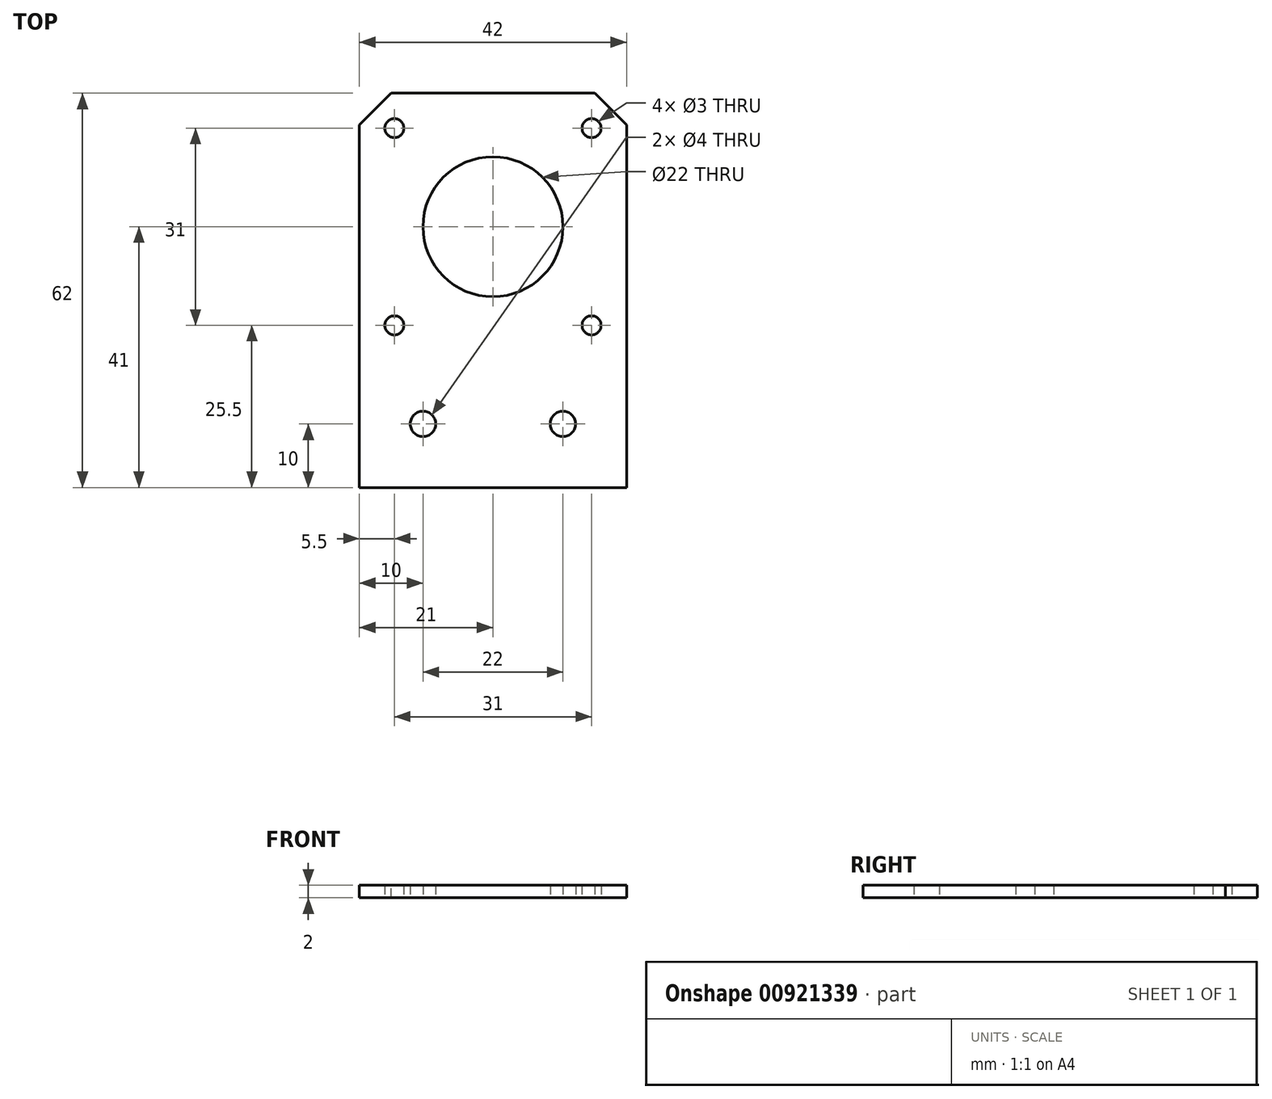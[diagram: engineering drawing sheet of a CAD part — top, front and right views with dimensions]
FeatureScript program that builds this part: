
annotation { "Feature Type Name" : "Feature", "Feature Type Description" : "" }
export const myFeature = defineFeature(function(context is Context, id is Id, definition is map)
    precondition{}
    {
        {
            var Q0;
            Q0=qCreatedBy(makeId("Top.planeOp"),FACE);
            var sketch = newSketch(context, id + "F0", { "sketchPlane" : qUnion([Q0])});
            skLineSegment(sketch, "E0.bottom", {"start": v(21, -31) * mm, "end": v(-21, -31) * mm});
            skLineSegment(sketch, "E0.top", {"start": v(21, 31) * mm, "end": v(-21, 31) * mm});
            skLineSegment(sketch, "E0.left", {"start": v(21, -31) * mm, "end": v(21, 31) * mm});
            skLineSegment(sketch, "E0.right", {"start": v(-21, -31) * mm, "end": v(-21, 31) * mm});
            skPoint(sketch, "E0.middle", {"position": v(0, 0) * mm});
            skCircle(sketch, "E1", {"center": v(-11, -21) * mm, "radius": 2 * mm});
            skCircle(sketch, "E2", {"center": v(11, -21) * mm, "radius": 2 * mm});
            skCircle(sketch, "E3", {"center": v(0, 10) * mm, "radius": 11 * mm});
            skCircle(sketch, "E4", {"center": v(15.5, 25.5) * mm, "radius": 1.5 * mm});
            skCircle(sketch, "E5", {"center": v(-15.5, 25.5) * mm, "radius": 1.5 * mm});
            skCircle(sketch, "E6", {"center": v(-15.5, -5.5) * mm, "radius": 1.5 * mm});
            skCircle(sketch, "E7", {"center": v(15.5, -5.5) * mm, "radius": 1.5 * mm});
            skSolve(sketch);
        }
        {
            var Q0;
            Q0=makeQuery(id+"F0.imprint","IMPRINT",FACE,{"disambiguationData":[TD([[makeQuery(id+"F0.imprint","IMPRINT",EDGE,{"derivedFrom":sQuery(id+"F0.wireOp",EDGE,"E0.bottom")}),-1.0]])]});
            extrude(context, id + "F1", {"entities" : qUnion([Q0]), "depth" : 2 * mm, "offsetDistance" : 25 * mm});
        }
        {
            var Q0;
            Q0=makeQuery(id+"F1.opExtrude","SWEPT_EDGE",EDGE,{"disambiguationData":[OSD([sQuery(id+"F0.wireOp",EDGE,"E0.top"),sQuery(id+"F0.wireOp",EDGE,"E0.left")])]});
            var Q1;
            Q1=makeQuery(id+"F1.opExtrude","SWEPT_EDGE",EDGE,{"disambiguationData":[OSD([sQuery(id+"F0.wireOp",EDGE,"E0.top"),sQuery(id+"F0.wireOp",EDGE,"E0.right")])]});
            chamfer(context, id + "F2", {"entities" : qUnion([Q0, Q1]), "width" : 5 * mm, "tangentPropagation" : true});
        }
    });
